# Revit family: IS_Ceraflex_B1717_BIM_DE
name_source: partatom
category: Plumbing Fixtures
revit_build: Autodesk Revit MEP 2014 (Build: 20130308_1515(x64)
units: mm (PartAtom-declared; Revit-internal decimal feet)

## types (1)
- B1717AA - Ceraflex single lever washbasin mixer wall mounted
    Accessories = www.idealstandard.de\ersatzteile
    AreaUnits = millimeters
    Assembly Code = C1030200
    AssetType = Fixed
    BIMObjectName = ISI_IdealStandard_WaterSupplyFittingsForWashBasinsAndTroughs_Ceraflex_B1717AA
    BREEAMApproved = No
    BarCode = 3800861055921
    Brand = Ideal Standard
    CWFU = 0
    CodePerformance = EN 817. DIN 4109. Gruppe 1
    Color = Chrome
    ConnectionType = Plumbing
    Cost = 0 $
    Default Elevation = 800 mm  [stored 2.62467 ft]
    Description = Ceraflex single lever washbasin mixer wall mounted
    DurationUnit = year
    ECA = No
    ExpectedLife = 25
    FaucetFunction = MIXED
    FaucetOperation = LEVERHANDLE
    FaucetType = PILLAR
    Features = Ceraflex single lever washbasin mixer wall mounted
    Finish = Chrome
    FlowRate = 18 Liters @ 3bar
    HWFU = 0
    IfcExportAs = IfcValveType
    IfcExportType = FAUCET
    InstallationInstructions = www.idealspec.co.uk/resources.html
    LinearUnits = millimeters
    ManufacturerURL = www.idealstandard.de
    Material = Brass
    Model = B1717AA
    ModelNumber = B1717AA
    NBSDescription = Water supply fittings for wash basins and troughs
    NBSReference = 45-35-70/371
    Name = WaterSupplyFittingsForWashBasinsAndTroughs_Ceraflex_B1717AA_IdealStandard
    NettWeight = 1.552 kg
    NominalHeight = 160 mm
    NominalLength = 217 mm
    NominalWidth = 220 mm  [stored 0.721785 ft]
    ProductInformation = www.idealstandard.de/produkte
    Shape = Sculptured
    Size = 220 x 217 x 160 mm
    Space = Internal
    SpareParts = www.idealstandard.de/ersatzteile
    TMV3 = Yes
    TestPressure = 10 Bar
    URL = www.idealstandard.com
    Uniclass2015Description = Washbasin taps
    Uniclass2015Reference = Pr_40_20_87_98
    Uniclass2015Version = Products v1.1
    ValveMechanism = ceramic disc
    ValveOperation = lever
    Version = 1
    VolumeUnits = Litres
    WFU = 0
    WRAS = Yes
    WaterEfficientProduct = No
    WorkingPressure = 1-5 Bar

note: [stored X ft] marks values corroborated as IEEE doubles in the binary element streams (Revit-internal decimal feet)

## geometry (parser evidence)
native form markers: Sweep x1
no freeform markers — native parametric forms only
